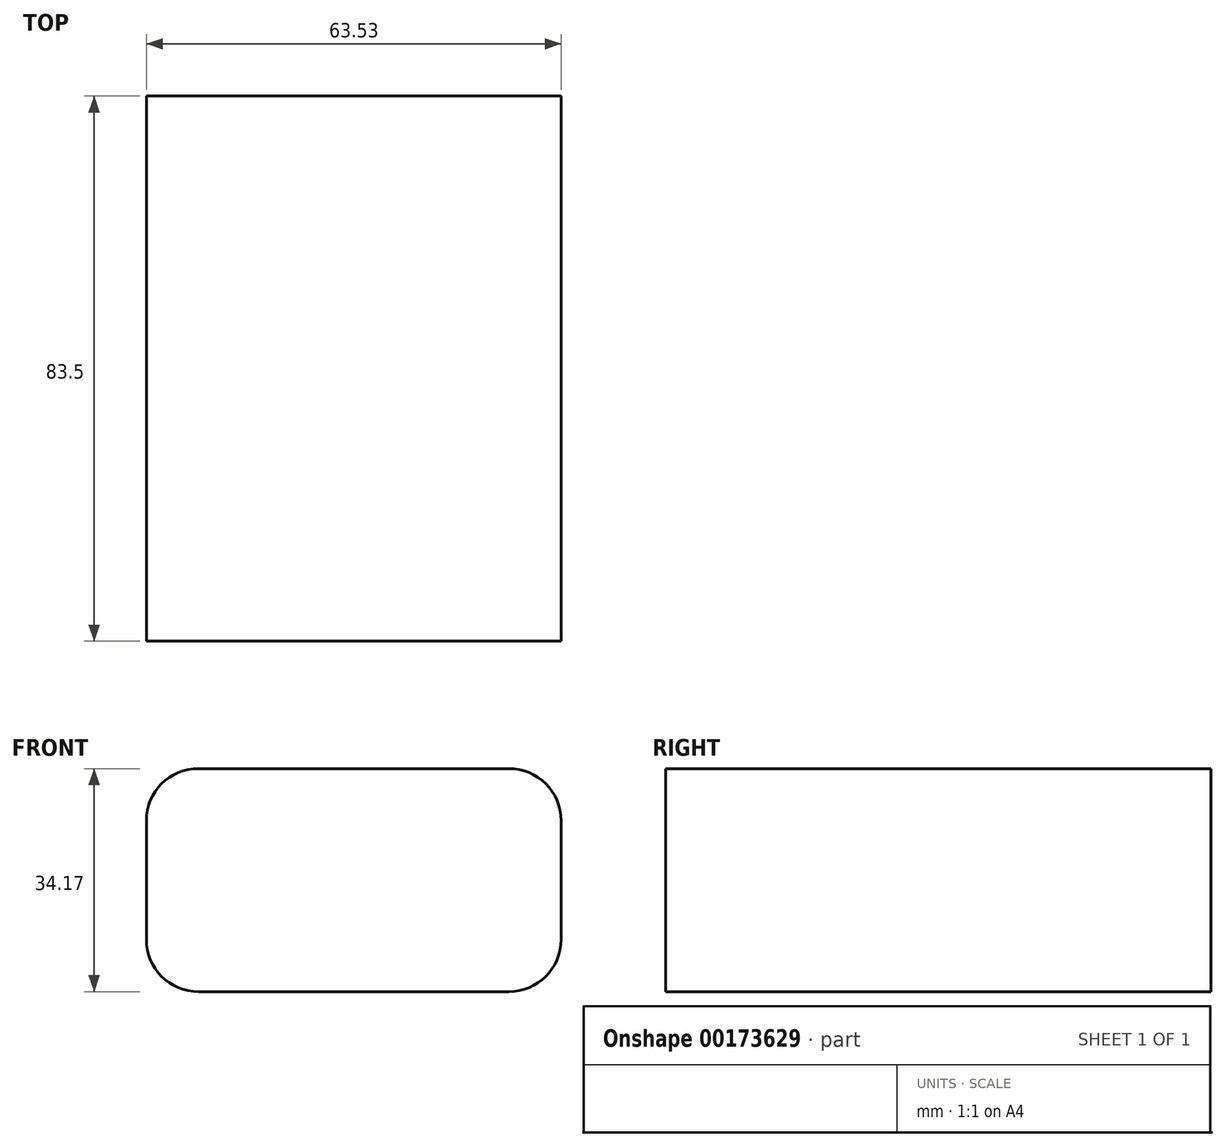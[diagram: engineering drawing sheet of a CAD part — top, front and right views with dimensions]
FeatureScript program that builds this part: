
annotation { "Feature Type Name" : "Feature", "Feature Type Description" : "" }
export const myFeature = defineFeature(function(context is Context, id is Id, definition is map)
    precondition{}
    {
        {
            var Q0;
            Q0=qCreatedBy(makeId("Front.planeOp"),FACE);
            var sketch = newSketch(context, id + "F0", { "sketchPlane" : qUnion([Q0])});
            skLineSegment(sketch, "E0.bottom", {"start": v(-8, 0) * mm, "end": v(-55.53, 0) * mm});
            skLineSegment(sketch, "E0.top", {"start": v(-8, -34.17) * mm, "end": v(-55.53, -34.17) * mm});
            skLineSegment(sketch, "E0.left", {"start": v(0, -8) * mm, "end": v(0, -26.17) * mm});
            skLineSegment(sketch, "E0.right", {"start": v(-63.53, -8) * mm, "end": v(-63.53, -26.17) * mm});
            skLineSegment(sketch, "E1.top", {"start": v(26.83, -44.09) * mm, "end": v(55.9, -44.09) * mm});
            skLineSegment(sketch, "E1.left", {"start": v(26.83, -19.54) * mm, "end": v(26.83, -44.09) * mm});
            skLineSegment(sketch, "E1.right", {"start": v(55.9, -19.54) * mm, "end": v(55.9, -44.09) * mm});
            skPoint(sketch, "E2.visualSharp", {"position": v(-63.53, 0) * mm});
            skArc(sketch, "E2.filletArc", {"start": v(-55.53, 0) * mm, "mid": v(-61.19, -2.34) * mm, "end": v(-63.53, -8) * mm});
            skPoint(sketch, "E3.visualSharp", {"position": v(0, -34.17) * mm});
            skArc(sketch, "E3.filletArc", {"start": v(-8, -34.17) * mm, "mid": v(-2.34, -31.83) * mm, "end": v(0, -26.17) * mm});
            skPoint(sketch, "E4.visualSharp", {"position": v(-63.53, -34.17) * mm});
            skArc(sketch, "E4.filletArc", {"start": v(-63.53, -26.17) * mm, "mid": v(-61.19, -31.83) * mm, "end": v(-55.53, -34.17) * mm});
            skPoint(sketch, "E5.visualSharp", {"position": v(0, 0) * mm});
            skArc(sketch, "E5.filletArc", {"start": v(0, -8) * mm, "mid": v(-2.34, -2.34) * mm, "end": v(-8, 0) * mm});
            skPoint(sketch, "E6.end.orphan", {"position": v(64.11, 0) * mm});
            skSolve(sketch);
        }
        {
            var Q0;
            Q0=qCreatedBy(makeId("Front.planeOp"),FACE);
            var sketch = newSketch(context, id + "F1", { "sketchPlane" : qUnion([Q0])});
            skFitSpline(sketch, "E7", {"points": [v(-59.49, 22.66) * mm, v(-51.56, 38.8) * mm, v(-32.3, 26.06) * mm, v(-21.53, 41.92) * mm, v(-2.83, 27.48) * mm, v(11.9, 43.9) * mm, v(30.03, 26.63) * mm, v(43.34, 43.34) * mm], "startDerivative": vector(38.82, 197.16) * mm, "endDerivative": vector(85.77, 199.14) * mm});
            skSolve(sketch);
        }
        {
            var Q0;
            Q0 = qSketchRegion(id + "F1", true);
            var Q1;
            Q1=makeQuery(id+"F0.imprint","IMPRINT",FACE,{"disambiguationData":[TD([[makeQuery(id+"F0.imprint","IMPRINT",EDGE,{"derivedFrom":sQuery(id+"F0.wireOp",EDGE,"E0.bottom")}),1.0]])]});
            extrude(context, id + "F2", {"entities" : qUnion([Q0, Q1]), "depth" : 83.5 * mm});
        }
    });
